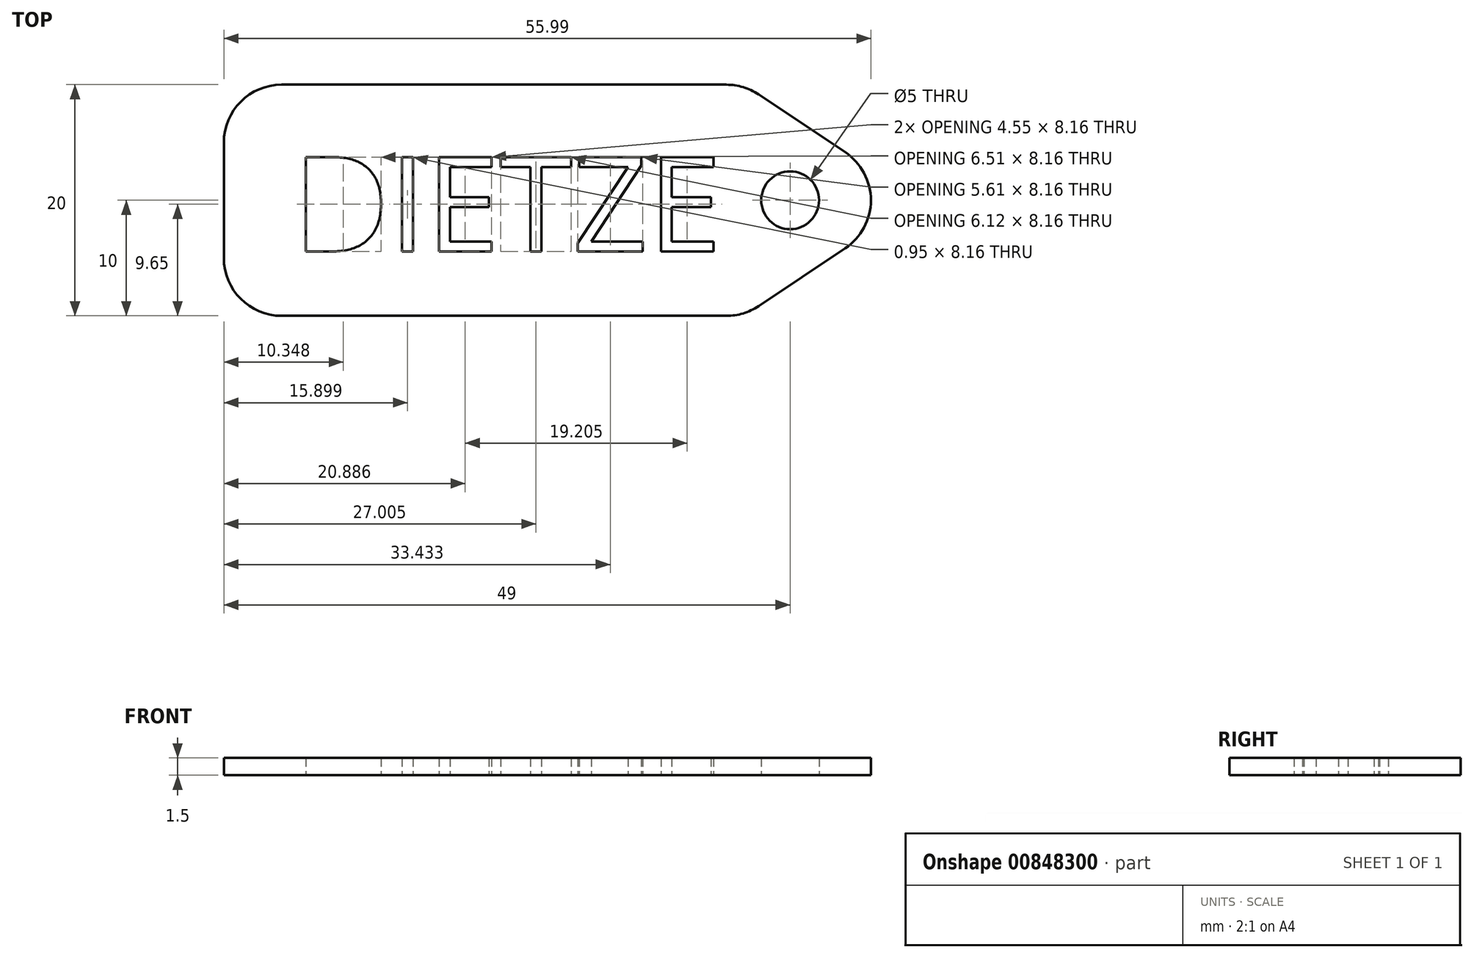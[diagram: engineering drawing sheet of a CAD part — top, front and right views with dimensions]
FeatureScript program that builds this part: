
annotation { "Feature Type Name" : "Feature", "Feature Type Description" : "" }
export const myFeature = defineFeature(function(context is Context, id is Id, definition is map)
    precondition{}
    {
        {
            var Q0;
            Q0=qCreatedBy(makeId("Top.planeOp"),FACE);
            var sketch = newSketch(context, id + "F0", { "sketchPlane" : qUnion([Q0])});
            skLineSegment(sketch, "E0.bottom", {"start": v(-60, 20) * mm, "end": v(-15, 20) * mm});
            skLineSegment(sketch, "E0.top", {"start": v(-60, 0) * mm, "end": v(0, 0) * mm});
            skLineSegment(sketch, "E0.left", {"start": v(-60, 20) * mm, "end": v(-60, 0) * mm});
            skLineSegment(sketch, "E1", {"start": v(-15, 20) * mm, "end": v(0, 10) * mm});
            skLineSegment(sketch, "E2", {"start": v(0, 10) * mm, "end": v(-15, 0) * mm});
            skPoint(sketch, "E3.orphan", {"position": v(0, 20) * mm});
            skText(sketch, "E4", { "text": "DIETZE", "fontName": "OpenSans-Regular.ttf"});
            skCircle(sketch, "E5", {"center": v(-11, 10) * mm, "radius": 2.5 * mm});
            const initialGuessF0  = {"E4": [-0.05403, 0.00557, 1, 0, 0.00823]};
            skSetInitialGuess(sketch, initialGuessF0);
            skSolve(sketch);
        }
        {
            var Q0;
            Q0=makeQuery(id+"F0.imprint","IMPRINT",FACE,{"disambiguationData":[TD([[makeQuery(id+"F0.imprint","IMPRINT",EDGE,{"derivedFrom":sQuery(id+"F0.wireOp",EDGE,"E0.bottom")}),-1.0]])]});
            extrude(context, id + "F1", {"entities" : qUnion([Q0]), "depth" : 1.5 * mm, "offsetDistance" : 25 * mm});
        }
        {
            var Q0;
            Q0=makeQuery(id+"F1.opExtrude","SWEPT_EDGE",EDGE,{"disambiguationData":[OSD([sQuery(id+"F0.wireOp",EDGE,"E1"),sQuery(id+"F0.wireOp",EDGE,"E2")])]});
            fillet(context, id + "F2", {"entities" : qUnion([Q0]), "radius" : 5 * mm, "tangentPropagation" : true, "allowEdgeOverflow" : false});
        }
        {
            var Q0;
            Q0=makeQuery(id+"F1.opExtrude","SWEPT_EDGE",EDGE,{"disambiguationData":[OSD([sQuery(id+"F0.wireOp",EDGE,"E0.bottom"),sQuery(id+"F0.wireOp",EDGE,"E0.left")])]});
            var Q1;
            Q1=makeQuery(id+"F1.opExtrude","SWEPT_EDGE",EDGE,{"disambiguationData":[OSD([sQuery(id+"F0.wireOp",EDGE,"E0.top"),sQuery(id+"F0.wireOp",EDGE,"E0.left")])]});
            var Q2;
            Q2=makeQuery(id+"F1.opExtrude","SWEPT_EDGE",EDGE,{"disambiguationData":[OSD([sQuery(id+"F0.wireOp",EDGE,"E0.top"),sQuery(id+"F0.wireOp",EDGE,"E2")])]});
            var Q3;
            Q3=makeQuery(id+"F1.opExtrude","SWEPT_EDGE",EDGE,{"disambiguationData":[OSD([sQuery(id+"F0.wireOp",EDGE,"E0.bottom"),sQuery(id+"F0.wireOp",EDGE,"E1")])]});
            fillet(context, id + "F3", {"entities" : qUnion([Q0, Q1, Q2, Q3]), "radius" : 5 * mm, "tangentPropagation" : true, "allowEdgeOverflow" : false});
        }
    });
